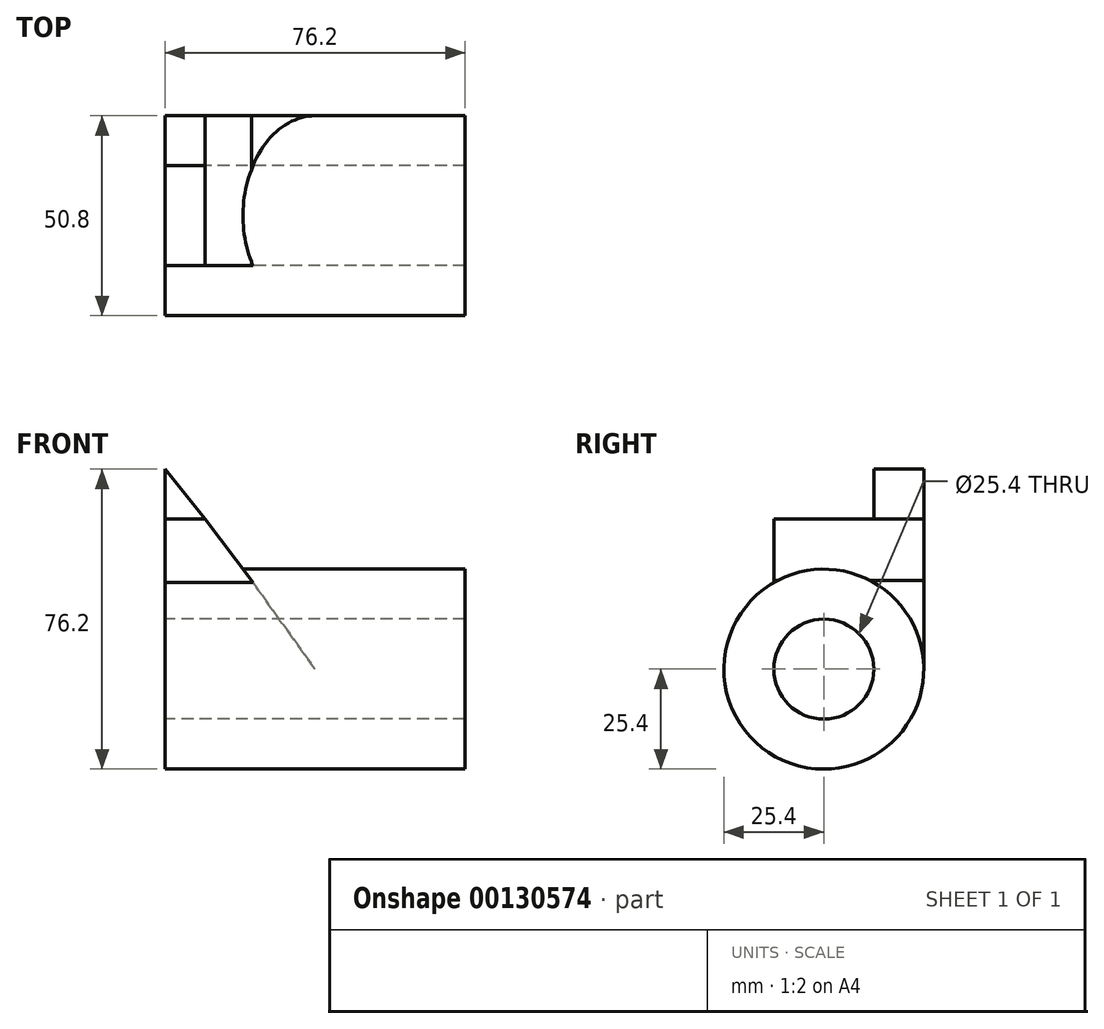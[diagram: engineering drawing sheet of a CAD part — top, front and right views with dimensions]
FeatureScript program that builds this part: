
annotation { "Feature Type Name" : "Feature", "Feature Type Description" : "" }
export const myFeature = defineFeature(function(context is Context, id is Id, definition is map)
    precondition{}
    {
        {
            var Q0;
            Q0=qCreatedBy(makeId("Right.planeOp"),FACE);
            var sketch = newSketch(context, id + "F0", { "sketchPlane" : qUnion([Q0])});
            skCircle(sketch, "E0", {"center": v(0, 0) * mm, "radius": 12.7 * mm});
            skCircle(sketch, "E1", {"center": v(0, 0) * mm, "radius": 25.4 * mm});
            skSolve(sketch);
        }
        {
            var Q0;
            Q0=makeQuery(id+"F0.imprint","IMPRINT",FACE,{"disambiguationData":[TD([[makeQuery(id+"F0.imprint","IMPRINT",EDGE,{"derivedFrom":sQuery(id+"F0.wireOp",EDGE,"E0")}),-1.0]])]});
            extrude(context, id + "F1", {"entities" : qUnion([Q0]), "depth" : 76.2 * mm});
        }
        {
            var Q0;
            Q0=qCreatedBy(makeId("Front.planeOp"),FACE);
            var sketch = newSketch(context, id + "F2", { "sketchPlane" : qUnion([Q0])});
            skLineSegment(sketch, "E2", {"start": v(0, 0) * mm, "end": v(0, 50.8) * mm});
            skLineSegment(sketch, "E3", {"start": v(0, 50.8) * mm, "end": v(10.16, 38.1) * mm});
            skLineSegment(sketch, "E4", {"start": v(10.16, 38.1) * mm, "end": v(0, 38.1) * mm});
            skLineSegment(sketch, "E5", {"start": v(10.16, 38.1) * mm, "end": v(21.91, 22.57) * mm});
            skLineSegment(sketch, "E6", {"start": v(21.91, 22.57) * mm, "end": v(0, 22.57) * mm});
            skLineSegment(sketch, "E7", {"start": v(21.91, 22.57) * mm, "end": v(38.1, 0) * mm});
            skLineSegment(sketch, "E8", {"start": v(38.1, 0) * mm, "end": v(0, 0) * mm});
            skSolve(sketch);
        }
        {
            var Q0;
            {var subQ0=sQuery(id+"F2.wireOp",EDGE,"E3");Q0=makeQuery(id+"F2.imprint","IMPRINT",FACE,{"disambiguationData":[TD([[makeQuery(id+"F2.imprint","IMPRINT",EDGE,{"derivedFrom":subQ0}),-1.0]])]});}
            extrude(context, id + "F3", {"entities" : qUnion([Q0]), "oppositeDirection" : true, "depth" : 25.4 * mm, "hasSecondDirection" : true, "secondDirectionOppositeDirection" : true, "secondDirectionDepth" : 12.7 * mm});
        }
        {
            var Q0;
            {var subQ0=sQuery(id+"F2.wireOp",EDGE,"E4");Q0=makeQuery(id+"F2.imprint","IMPRINT",FACE,{"disambiguationData":[TD([[makeQuery(id+"F2.imprint","IMPRINT",EDGE,{"derivedFrom":subQ0}),1.0]])]});}
            extrude(context, id + "F4", {"entities" : qUnion([Q0]), "operationType" : NewBodyOperationType.ADD, "depth" : 12.7 * mm, "hasSecondDirection" : true, "secondDirectionOppositeDirection" : true, "secondDirectionDepth" : 25.4 * mm});
        }
        {
            var Q0;
            {var subQ2=sQuery(id+"F2.wireOp",EDGE,"E6");Q0=makeQuery(id+"F2.imprint","IMPRINT",FACE,{"disambiguationData":[TD([[makeQuery(id+"F2.imprint","IMPRINT",EDGE,{"derivedFrom":subQ2}),1.0]])]});}
            extrude(context, id + "F5", {"entities" : qUnion([Q0]), "operationType" : NewBodyOperationType.ADD, "depth" : 12.7 * mm, "hasSecondDirection" : true, "secondDirectionOppositeDirection" : true, "secondDirectionDepth" : 25.4 * mm});
        }
        {
            var Q0;
            Q0=makeQuery(id+"F0.imprint","IMPRINT",FACE,{"disambiguationData":[TD([[makeQuery(id+"F0.imprint","IMPRINT",EDGE,{"derivedFrom":sQuery(id+"F0.wireOp",EDGE,"E0")}),1.0]])]});
            extrude(context, id + "F6", {"entities" : qUnion([Q0]), "operationType" : NewBodyOperationType.REMOVE, "endBound" : BoundingType.THROUGH_ALL, "depth" : 25.4 * mm});
        }
    });
